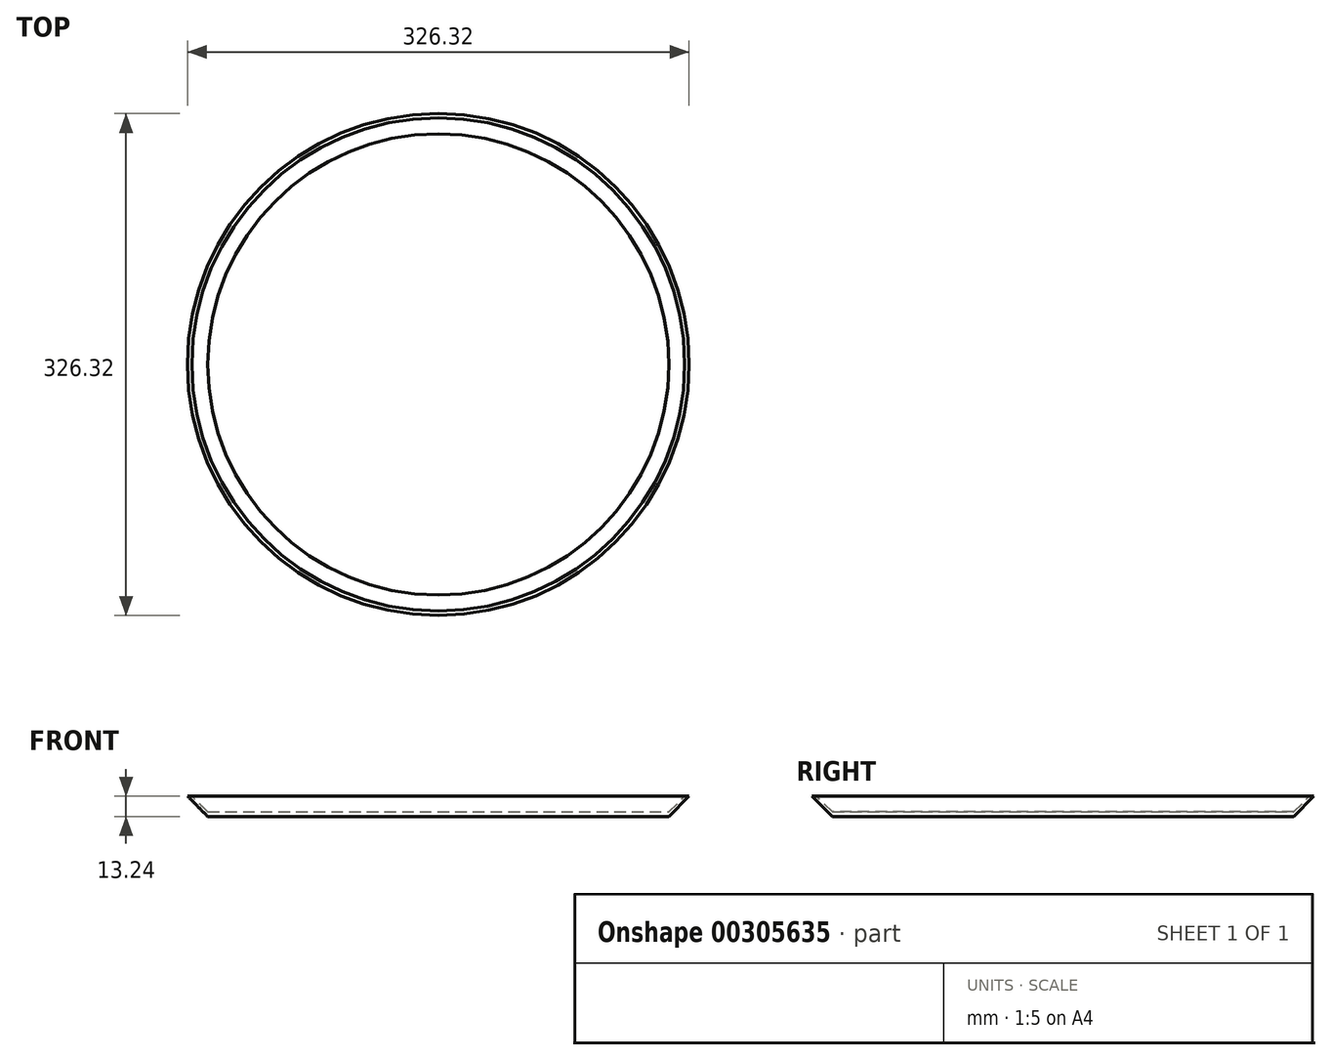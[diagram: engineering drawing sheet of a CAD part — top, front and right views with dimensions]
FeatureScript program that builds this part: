
annotation { "Feature Type Name" : "Feature", "Feature Type Description" : "" }
export const myFeature = defineFeature(function(context is Context, id is Id, definition is map)
    precondition{}
    {
        {
            var Q0;
            Q0=qCreatedBy(makeId("Front.planeOp"),FACE);
            var sketch = newSketch(context, id + "F0", { "sketchPlane" : qUnion([Q0])});
            skLineSegment(sketch, "E0", {"start": v(0, 0) * mm, "end": v(150, 0) * mm});
            skLineSegment(sketch, "E1", {"start": v(0, 0) * mm, "end": v(0, 14.55) * mm});
            skLineSegment(sketch, "E2", {"start": v(150, 0) * mm, "end": v(163.16, 13.24) * mm});
            skLineSegment(sketch, "E3.0", {"start": v(0, 3) * mm, "end": v(150, 3) * mm});
            skLineSegment(sketch, "E4", {"start": v(150, 3) * mm, "end": v(160.29, 13.24) * mm});
            skLineSegment(sketch, "E5", {"start": v(160.29, 13.24) * mm, "end": v(163.16, 13.24) * mm});
            skSolve(sketch);
        }
        {
            var Q0;
            Q0 = qSketchRegion(id + "F0", true);
            var Q1;
            Q1=sQuery(id+"F0.wireOp",EDGE,"E1");
            revolve(context, id + "F1", {"entities" : qUnion([Q0]), "axis" : qUnion([Q1]), "revolveType" : RevolveType.FULL});
        }
    });
